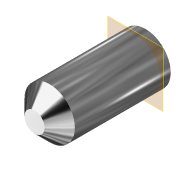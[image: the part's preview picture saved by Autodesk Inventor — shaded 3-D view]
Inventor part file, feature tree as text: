
AUTODESK INVENTOR PART (.ipt)
format: ipt  version: 2022 (Build 260153000, 153)  size: 108,032 bytes
history: native  units: mm
features: extrude x2, sketch x2, plane x1, chamfer x1
ambient origin geometry x8: Origin, YZ Plane, XZ Plane, XY Plane, X Axis, Y Axis, Z Axis, Center Point
bodies: Solid1 (feature_tree)
feature tree (6):
  plane  "Work Plane3"
  extrude  "Extrusion1"  Depth=40.0mm TaperAngle=0.0deg
  chamfer  "Chamfer2"  Distance=6.0mm Angle=45.0deg
  extrude  "Extrusion2"  Depth=4.0mm TaperAngle=0.0deg
  sketch  "Sketch2"  dims[d0=20.0mm d1=40.0mm d2=0.0mm d6=6.0mm d7=2.0mm d8=45.0deg]
  sketch  "Sketch3"  dims[d9=20.0mm d10=4.0mm d11=0.0mm]
